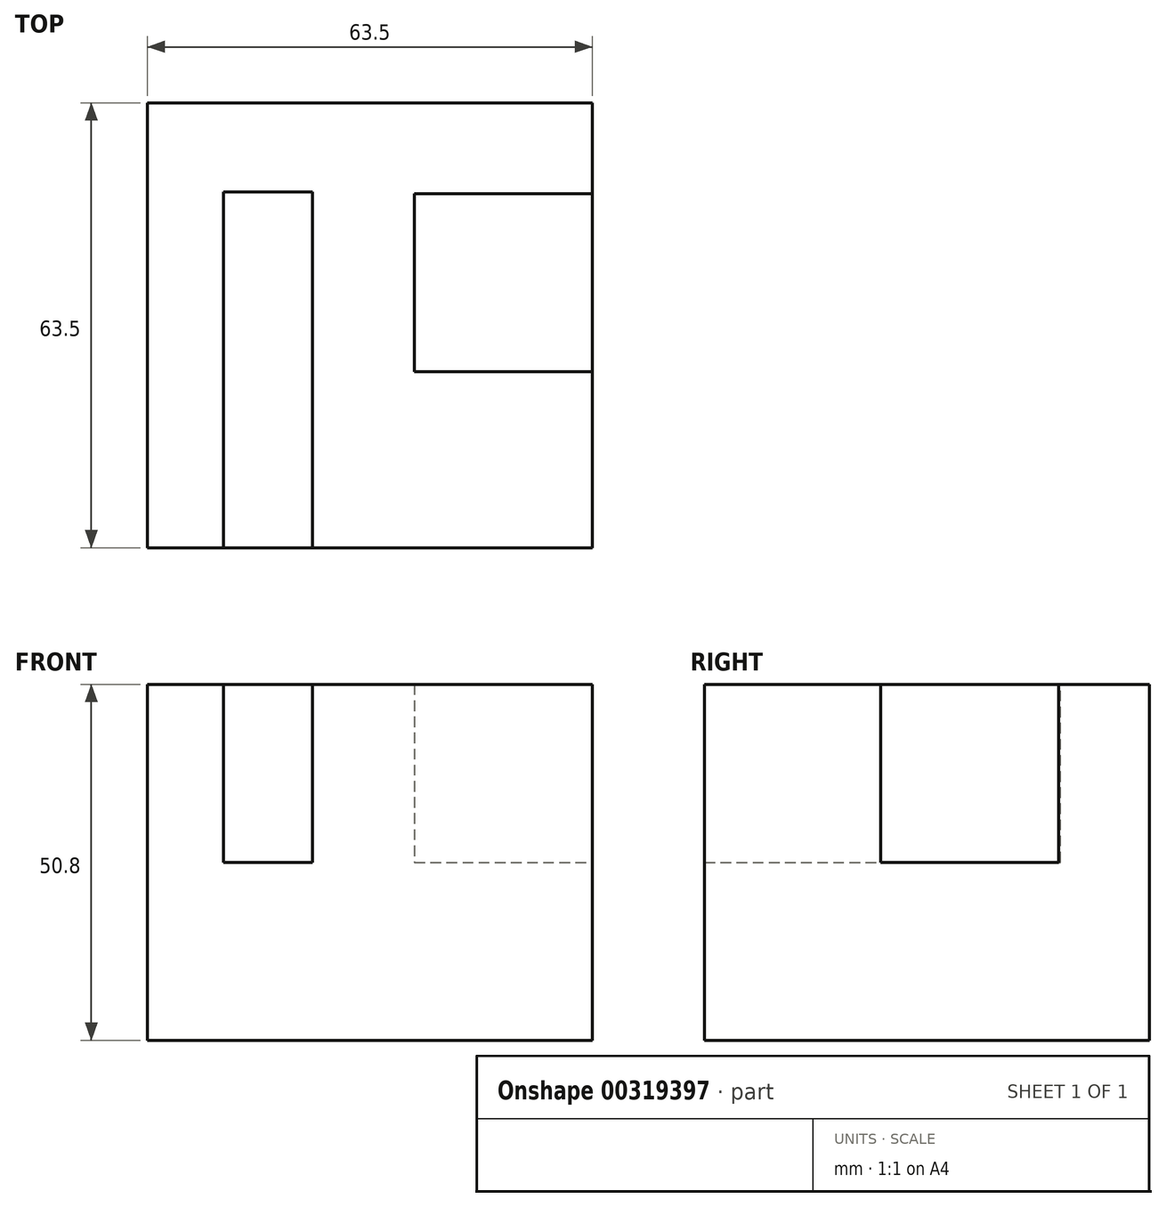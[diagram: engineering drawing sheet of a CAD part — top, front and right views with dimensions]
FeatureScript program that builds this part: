
annotation { "Feature Type Name" : "Feature", "Feature Type Description" : "" }
export const myFeature = defineFeature(function(context is Context, id is Id, definition is map)
    precondition{}
    {
        {
            var Q0;
            Q0=qCreatedBy(makeId("Front.planeOp"),FACE);
            var sketch = newSketch(context, id + "F0", { "sketchPlane" : qUnion([Q0])});
            skLineSegment(sketch, "E0", {"start": v(-44.6, -45.03) * mm, "end": v(18.9, -45.03) * mm});
            skLineSegment(sketch, "E1", {"start": v(18.9, -45.03) * mm, "end": v(18.9, 5.77) * mm});
            skLineSegment(sketch, "E2", {"start": v(18.9, 5.77) * mm, "end": v(-44.6, 5.77) * mm});
            skLineSegment(sketch, "E3", {"start": v(-44.6, 5.77) * mm, "end": v(-44.6, -45.03) * mm});
            skSolve(sketch);
        }
        {
            var Q0;
            Q0=makeQuery(id+"F0.imprint","IMPRINT",FACE,{"disambiguationData":[TD([[makeQuery(id+"F0.imprint","IMPRINT",EDGE,{"derivedFrom":sQuery(id+"F0.wireOp",EDGE,"E0")}),1.0]])]});
            extrude(context, id + "F1", {"entities" : qUnion([Q0]), "depth" : 63.5 * mm});
        }
        {
            var Q0;
            Q0=makeQuery(id+"F1.opExtrude","SWEPT_FACE",FACE,{"disambiguationData":[OSD([sQuery(id+"F0.wireOp",EDGE,"E2")])]});
            var sketch = newSketch(context, id + "F2", { "sketchPlane" : qUnion([Q0])});
            skLineSegment(sketch, "E4", {"start": v(-33.74, -63.5) * mm, "end": v(-33.74, -12.7) * mm});
            skLineSegment(sketch, "E5", {"start": v(-33.74, -12.7) * mm, "end": v(-21.04, -12.7) * mm});
            skLineSegment(sketch, "E6", {"start": v(-21.04, -12.7) * mm, "end": v(-21.04, -63.5) * mm});
            skSolve(sketch);
        }
        {
            var Q0;
            {var subQ0=sQuery(id+"F2.wireOp",EDGE,"E4");Q0=makeQuery(id+"F2.imprint","IMPRINT",FACE,{"disambiguationData":[TD([[makeQuery(id+"F2.imprint","IMPRINT",EDGE,{"derivedFrom":subQ0}),-1.0]])]});}
            extrude(context, id + "F3", {"entities" : qUnion([Q0]), "operationType" : NewBodyOperationType.REMOVE, "oppositeDirection" : true, "depth" : 25.4 * mm});
        }
        {
            var Q0;
            Q0=makeQuery(id+"F1.opExtrude","SWEPT_FACE",FACE,{"disambiguationData":[OSD([sQuery(id+"F0.wireOp",EDGE,"E1")])]});
            var sketch = newSketch(context, id + "F4", { "sketchPlane" : qUnion([Q0])});
            skLineSegment(sketch, "E7", {"start": v(-12.98, 5.77) * mm, "end": v(-12.98, -19.63) * mm});
            skLineSegment(sketch, "E8", {"start": v(-12.98, -19.63) * mm, "end": v(-38.38, -19.63) * mm});
            skLineSegment(sketch, "E9", {"start": v(-38.38, -19.63) * mm, "end": v(-38.38, 5.77) * mm});
            skSolve(sketch);
        }
        {
            var Q0;
            {var subQ0=sQuery(id+"F4.wireOp",EDGE,"E7");Q0=makeQuery(id+"F4.imprint","IMPRINT",FACE,{"disambiguationData":[TD([[makeQuery(id+"F4.imprint","IMPRINT",EDGE,{"derivedFrom":subQ0}),-1.0]])]});}
            extrude(context, id + "F5", {"entities" : qUnion([Q0]), "operationType" : NewBodyOperationType.REMOVE, "oppositeDirection" : true, "depth" : 25.4 * mm});
        }
    });
